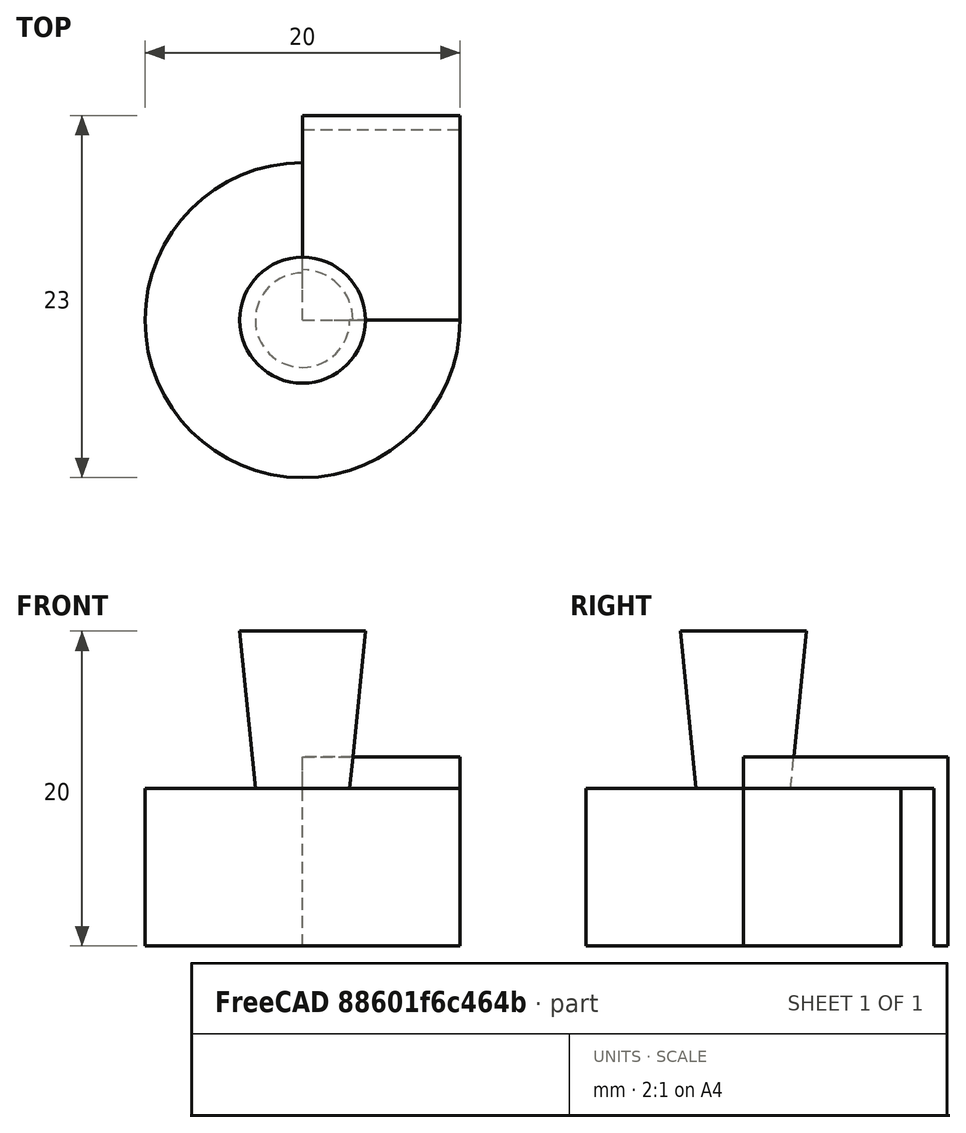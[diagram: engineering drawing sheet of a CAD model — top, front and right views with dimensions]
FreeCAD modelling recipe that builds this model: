
FCSTD DOCUMENT  (FreeCAD 0.17R13522 (Git))
Label: PartDesignPrimitives
License: All rights reserved
LicenseURL: http://en.wikipedia.org/wiki/All_rights_reserved
objects: Part::Cone×1, PartDesign::FeatureBase×1, PartDesign::AdditiveCylinder×1, PartDesign::AdditiveBox×1, PartDesign::SubtractiveBox×1, PartDesign::Body×1
note: 9 computed .brp shape members not serialized (recipe doc carries the construction recipe); baked Part::Feature solids carry a one-line shape summary decoded from their .brp

FEATURE [Part::Cone] Cone
  Angle = 360
  AttacherType = Attacher::AttachEngine3D
  Height = 20
  Radius1 = 2
  Radius2 = 4
FEATURE [PartDesign::FeatureBase] BaseFeature
  BaseFeature = -> Cone
FEATURE [PartDesign::AdditiveCylinder] Cylinder  label="PrimitiveAdditiveCylinder1"
  Angle = 360
  AttacherType = Attacher::AttachEngine3D
  BaseFeature = -> BaseFeature
  Height = 10
  Radius = 10
FEATURE [PartDesign::AdditiveBox] Box  label="PrimitiveAdditiveBox1"
  AttacherType = Attacher::AttachEngine3D
  BaseFeature = -> Cylinder
  Height = 12
  Length = 10
  Width = 13
FEATURE [PartDesign::SubtractiveBox] Box001  label="PrimitiveSubtractiveBox1"
  AttacherType = Attacher::AttachEngine3D
  BaseFeature = -> Box
  Height = 10
  Length = 10.1
  Width = 12.1
FEATURE [PartDesign::Body] Body
  BaseFeature = -> Cone
  Group = -> [BaseFeature,Cylinder,Box,Box001]
  Origin = -> Origin
  Tip = -> Box001
